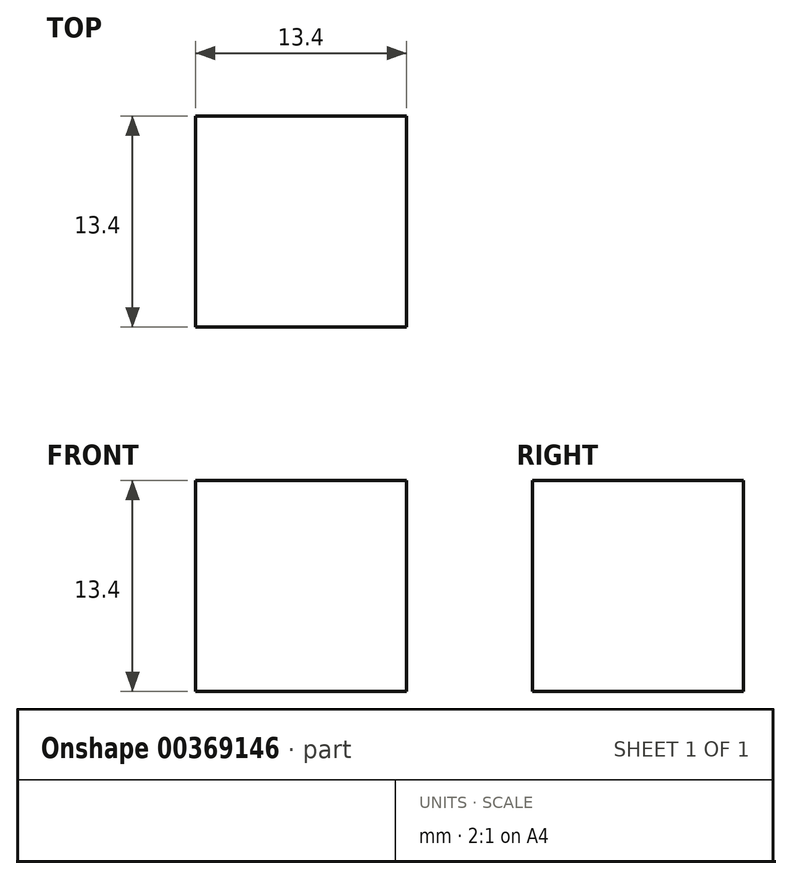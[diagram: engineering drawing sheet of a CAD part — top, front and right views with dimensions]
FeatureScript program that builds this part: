
annotation { "Feature Type Name" : "Feature", "Feature Type Description" : "" }
export const myFeature = defineFeature(function(context is Context, id is Id, definition is map)
    precondition{}
    {
        {
            var Q0;
            Q0=qCreatedBy(makeId("Front.planeOp"),FACE);
            var sketch = newSketch(context, id + "F0", { "sketchPlane" : qUnion([Q0])});
            skLineSegment(sketch, "E0.bottom", {"start": v(6.7, 6.7) * mm, "end": v(-6.7, 6.7) * mm});
            skLineSegment(sketch, "E0.top", {"start": v(6.7, -6.7) * mm, "end": v(-6.7, -6.7) * mm});
            skLineSegment(sketch, "E0.left", {"start": v(6.7, 6.7) * mm, "end": v(6.7, -6.7) * mm});
            skLineSegment(sketch, "E0.right", {"start": v(-6.7, 6.7) * mm, "end": v(-6.7, -6.7) * mm});
            skPoint(sketch, "E0.middle", {"position": v(0, 0) * mm});
            skSolve(sketch);
        }
        {
            var Q0;
            Q0=makeQuery(id+"F0.imprint","IMPRINT",FACE,{"disambiguationData":[TD([[makeQuery(id+"F0.imprint","IMPRINT",EDGE,{"derivedFrom":sQuery(id+"F0.wireOp",EDGE,"E0.bottom")}),1.0]])]});
            extrude(context, id + "F1", {"entities" : qUnion([Q0]), "endBound" : BoundingType.SYMMETRIC, "depth" : 13.4 * mm});
        }
    });
